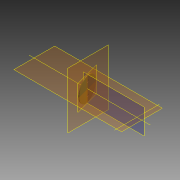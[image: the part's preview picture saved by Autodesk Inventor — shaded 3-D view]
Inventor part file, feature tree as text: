
AUTODESK INVENTOR PART (.ipt)
format: ipt  version: 2015 (Build 190159000, 159)  size: 127,488 bytes
history: native  units: mm
features: plane x3, extrude x3, sketch x3, other x1, reference x1
ambient origin geometry x8: Origin, YZ Plane, XZ Plane, XY Plane, X Axis, Y Axis, Z Axis, Center Point
bodies: Solid1 (feature_tree)
feature tree (11):
  plane  "Work Plane1"
  extrude  "Extrusion1"  Depth=1.0mm
  plane  "Work Plane2"
  extrude  "Extrusion2"  Depth=30.0mm TaperAngle=0.0deg
  other  "Work Axis1"
  plane  "Work Plane3"
  extrude  "Extrusion3"  Depth=7.5mm
  sketch  "Sketch1"  dims[d1=15.0deg d2=1.0mm]
  sketch  "Sketch2"  dims[d3=30.0mm d4=30.0mm d5=0.0mm d6=0.0mm d7=30.0mm d8=0.0mm]
  sketch  "Sketch4"  dims[d11=7.5mm d12=7.5mm d20=3.0mm d21=3.0mm d22=30.0mm d23=15.0mm d24=0.0mm d25=0.0mm]
  reference  "Reference2"
